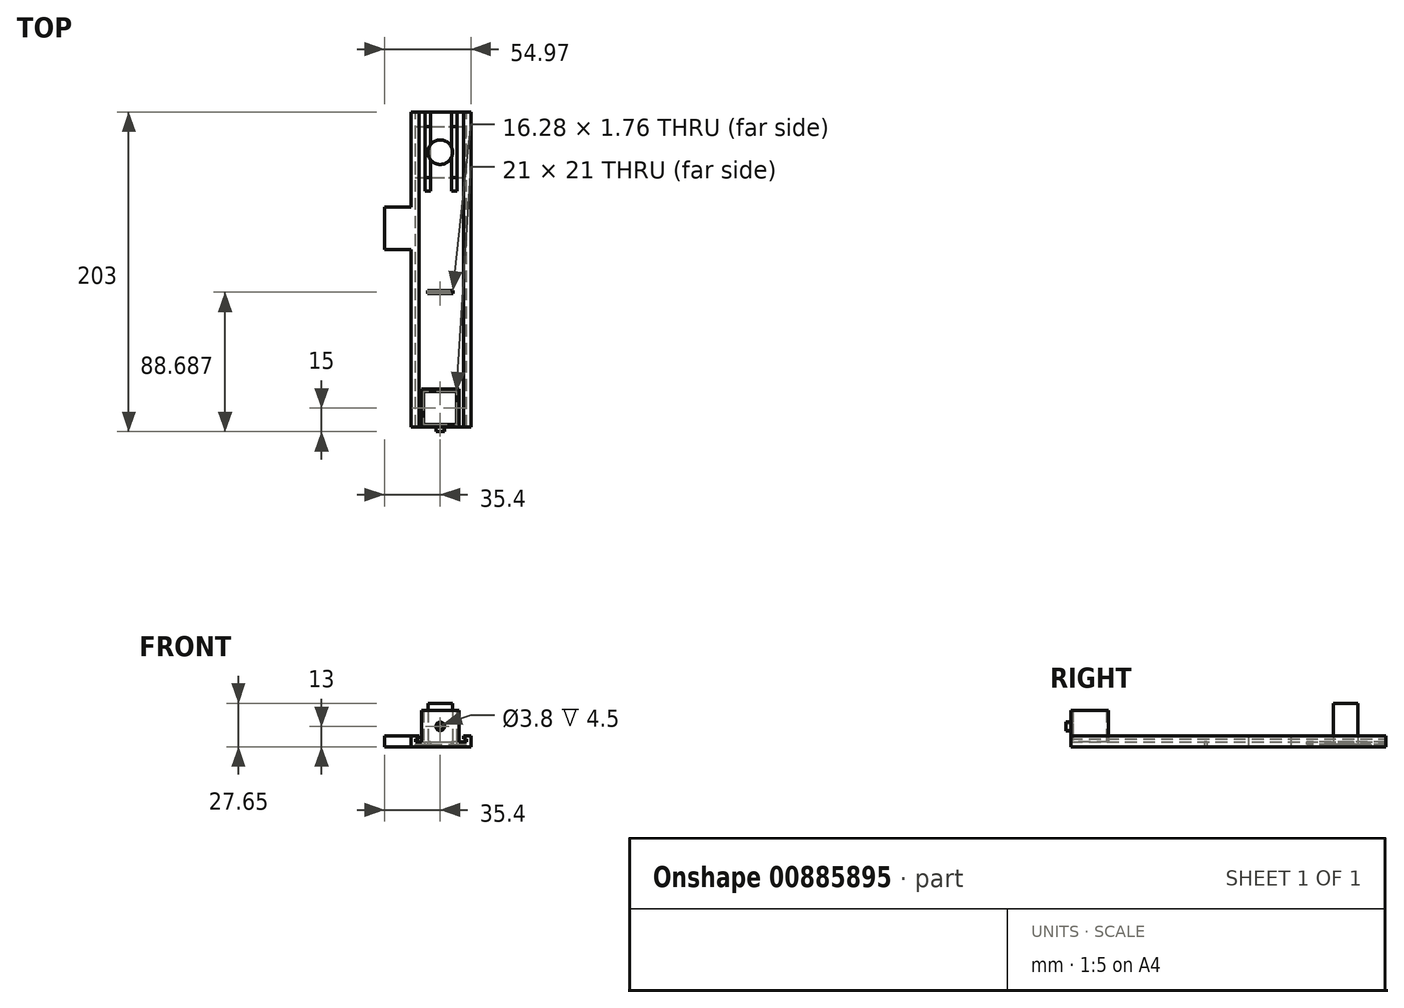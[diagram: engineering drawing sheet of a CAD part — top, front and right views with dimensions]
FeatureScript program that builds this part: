
annotation { "Feature Type Name" : "Feature", "Feature Type Description" : "" }
export const myFeature = defineFeature(function(context is Context, id is Id, definition is map)
    precondition{}
    {
        {
            var Q0;
            Q0=qCreatedBy(makeId("Top.planeOp"),FACE);
            var sketch = newSketch(context, id + "F0", { "sketchPlane" : qUnion([Q0])});
            skLineSegment(sketch, "E0.bottom", {"start": v(-16.12, 16.11) * mm, "end": v(16.13, 16.11) * mm});
            skLineSegment(sketch, "E0.top", {"start": v(-16.13, -16.11) * mm, "end": v(16.12, -16.11) * mm});
            skLineSegment(sketch, "E0.left", {"start": v(-16.12, 16.11) * mm, "end": v(-16.13, -16.11) * mm});
            skLineSegment(sketch, "E0.right", {"start": v(16.13, 16.11) * mm, "end": v(16.12, -16.11) * mm});
            skPoint(sketch, "E0.middle", {"position": v(0, 0) * mm});
            skSolve(sketch);
        }
        {
            var Q0;
            Q0=makeQuery(id+"F0.imprint","IMPRINT",FACE,{"disambiguationData":[TD([[makeQuery(id+"F0.imprint","IMPRINT",EDGE,{"derivedFrom":sQuery(id+"F0.wireOp",EDGE,"E0.bottom")}),-1.0]])]});
            extrude(context, id + "F1", {"entities" : qUnion([Q0]), "depth" : 1.65 * mm, "offsetDistance" : 25 * mm});
        }
        {
            var Q0;
            Q0=makeQuery(id+"F1.opExtrude","CAP_FACE",FACE,{"disambiguationData":[OSD([sQuery(id+"F0.wireOp",EDGE,"E0.bottom"),sQuery(id+"F0.wireOp",EDGE,"E0.top"),sQuery(id+"F0.wireOp",EDGE,"E0.left"),sQuery(id+"F0.wireOp",EDGE,"E0.right")])],"isStart":false});
            var sketch = newSketch(context, id + "F2", { "sketchPlane" : qUnion([Q0])});
            skCircle(sketch, "E1", {"center": v(0, 0) * mm, "radius": 7.8 * mm});
            skSolve(sketch);
        }
        {
            var Q0;
            Q0=makeQuery(id+"F2.imprint","IMPRINT",FACE,{"disambiguationData":[TD([[makeQuery(id+"F2.imprint","IMPRINT",EDGE,{"derivedFrom":sQuery(id+"F2.wireOp",EDGE,"E1")}),1.0]])]});
            extrude(context, id + "F3", {"entities" : qUnion([Q0]), "operationType" : NewBodyOperationType.ADD, "depth" : 26 * mm, "offsetDistance" : 25 * mm});
        }
        {
            var Q0;
            Q0=qCreatedBy(makeId("Top.planeOp"),FACE);
            var sketch = newSketch(context, id + "F4", { "sketchPlane" : qUnion([Q0])});
            skLineSegment(sketch, "E2.bottom", {"start": v(-18.43, 25.4) * mm, "end": v(19.57, 25.4) * mm});
            skLineSegment(sketch, "E2.top", {"start": v(-18.43, -174.6) * mm, "end": v(19.57, -174.6) * mm});
            skLineSegment(sketch, "E2.left", {"start": v(-18.43, 25.4) * mm, "end": v(-18.43, -174.6) * mm});
            skLineSegment(sketch, "E2.right", {"start": v(19.57, 25.4) * mm, "end": v(19.57, -174.6) * mm});
            skSolve(sketch);
        }
        {
            var Q0;
            Q0=makeQuery(id+"F4.imprint","IMPRINT",FACE,{"disambiguationData":[TD([[makeQuery(id+"F4.imprint","IMPRINT",EDGE,{"derivedFrom":sQuery(id+"F4.wireOp",EDGE,"E2.bottom")}),-1.0]])]});
            extrude(context, id + "F5", {"entities" : qUnion([Q0]), "depth" : 3 * mm, "offsetDistance" : 25 * mm});
        }
        {
            var Q0;
            Q0=makeQuery(id+"F5.opExtrude","SWEPT_FACE",FACE,{"disambiguationData":[OSD([sQuery(id+"F4.wireOp",EDGE,"E2.bottom")])]});
            var sketch = newSketch(context, id + "F6", { "sketchPlane" : qUnion([Q0])});
            skLineSegment(sketch, "E3", {"start": v(-0.57, -1.9) * mm, "end": v(-0.57, 4.44) * mm, "construction": true});
            skPoint(sketch, "E3.startSnap0", {"position": v(-0.57, 0) * mm});
            skLineSegment(sketch, "E4", {"start": v(-0.57, 3) * mm, "end": v(-16.72, 3) * mm});
            skLineSegment(sketch, "E5", {"start": v(-16.72, 3) * mm, "end": v(-16.72, 5) * mm});
            skLineSegment(sketch, "E6", {"start": v(-16.72, 5) * mm, "end": v(-14.72, 5) * mm});
            skLineSegment(sketch, "E7", {"start": v(-14.72, 5) * mm, "end": v(-14.72, 7) * mm});
            skLineSegment(sketch, "E8", {"start": v(-14.72, 7) * mm, "end": v(-19.57, 7) * mm});
            skLineSegment(sketch, "E9", {"start": v(-19.57, 7) * mm, "end": v(-19.57, 3) * mm});
            skLineSegment(sketch, "E10", {"start": v(-19.57, 3) * mm, "end": v(-16.72, 3) * mm});
            skLineSegment(sketch, "E11", {"start": v(-0.57, 3) * mm, "end": v(15.58, 3) * mm});
            skLineSegment(sketch, "E12", {"start": v(15.58, 3) * mm, "end": v(15.58, 5) * mm});
            skLineSegment(sketch, "E13", {"start": v(15.58, 5) * mm, "end": v(13.58, 5) * mm});
            skLineSegment(sketch, "E14", {"start": v(13.58, 5) * mm, "end": v(13.58, 7) * mm});
            skLineSegment(sketch, "E15", {"start": v(13.58, 7) * mm, "end": v(18.43, 7) * mm});
            skLineSegment(sketch, "E16", {"start": v(18.43, 7) * mm, "end": v(18.43, 3) * mm});
            skLineSegment(sketch, "E17", {"start": v(18.43, 3) * mm, "end": v(15.58, 3) * mm});
            skSolve(sketch);
        }
        {
            var Q0;
            Q0=makeQuery(id+"F6.imprint","IMPRINT",FACE,{"disambiguationData":[TD([[makeQuery(id+"F6.imprint","IMPRINT",EDGE,{"derivedFrom":sQuery(id+"F6.wireOp",EDGE,"E5")}),1.0]])]});
            var Q1;
            Q1=makeQuery(id+"F6.imprint","IMPRINT",FACE,{"disambiguationData":[TD([[makeQuery(id+"F6.imprint","IMPRINT",EDGE,{"derivedFrom":sQuery(id+"F6.wireOp",EDGE,"E12")}),-1.0]])]});
            var Q2;
            Q2=makeQuery(id+"F5.opExtrude","SWEPT_FACE",FACE,{"disambiguationData":[OSD([sQuery(id+"F4.wireOp",EDGE,"E2.top")])]});
            extrude(context, id + "F7", {"entities" : qUnion([Q0, Q1]), "operationType" : NewBodyOperationType.ADD, "endBound" : BoundingType.UP_TO_SURFACE, "oppositeDirection" : true, "depth" : 25 * mm, "endBoundEntityFace" : qUnion([Q2]), "offsetDistance" : 25 * mm});
        }
        {
            var Q0;
            Q0=makeQuery(id+"F5.opExtrude","CAP_FACE",FACE,{"disambiguationData":[OSD([sQuery(id+"F4.wireOp",EDGE,"E2.bottom"),sQuery(id+"F4.wireOp",EDGE,"E2.top"),sQuery(id+"F4.wireOp",EDGE,"E2.left"),sQuery(id+"F4.wireOp",EDGE,"E2.right")])],"isStart":false});
            var sketch = newSketch(context, id + "F8", { "sketchPlane" : qUnion([Q0])});
            skLineSegment(sketch, "E18", {"start": v(0, -174.6) * mm, "end": v(0, -150.6) * mm, "construction": true});
            skPoint(sketch, "E19.middle", {"position": v(0, -162.6) * mm});
            skLineSegment(sketch, "E20.bottom", {"start": v(-12, -150.6) * mm, "end": v(12, -150.6) * mm});
            skLineSegment(sketch, "E20.top", {"start": v(-12, -174.6) * mm, "end": v(12, -174.6) * mm});
            skLineSegment(sketch, "E20.left", {"start": v(-12, -150.6) * mm, "end": v(-12, -174.6) * mm});
            skLineSegment(sketch, "E20.right", {"start": v(12, -150.6) * mm, "end": v(12, -174.6) * mm});
            skLineSegment(sketch, "E21.bottom", {"start": v(-10.5, -152.1) * mm, "end": v(10.5, -152.1) * mm});
            skLineSegment(sketch, "E21.top", {"start": v(-10.5, -173.1) * mm, "end": v(10.5, -173.1) * mm});
            skLineSegment(sketch, "E21.left", {"start": v(-10.5, -152.1) * mm, "end": v(-10.5, -173.1) * mm});
            skLineSegment(sketch, "E21.right", {"start": v(10.5, -152.1) * mm, "end": v(10.5, -173.1) * mm});
            skSolve(sketch);
        }
        {
            var Q0;
            Q0=makeQuery(id+"F8.imprint","IMPRINT",FACE,{"disambiguationData":[TD([[makeQuery(id+"F8.imprint","IMPRINT",EDGE,{"derivedFrom":sQuery(id+"F8.wireOp",EDGE,"E20.bottom")}),-1.0]])]});
            extrude(context, id + "F9", {"entities" : qUnion([Q0]), "operationType" : NewBodyOperationType.ADD, "depth" : 20 * mm, "offsetDistance" : 25 * mm});
        }
        {
            var Q0;
            {var subQ6=sQuery(id+"F4.wireOp",EDGE,"E2.bottom");var subQ13=sQuery(id+"F4.wireOp",EDGE,"E2.top");Q0=makeQuery(id+"F9.boolean.opBoolean","SPLIT",FACE,{"disambiguationData":[TD([makeQuery(id+"F5.opExtrude","SWEPT_FACE",FACE,{"disambiguationData":[OSD([subQ6])]})])],"derivedFrom":makeQuery(id+"F5.opExtrude","CAP_FACE",FACE,{"disambiguationData":[OSD([subQ6,subQ13,sQuery(id+"F4.wireOp",EDGE,"E2.left"),sQuery(id+"F4.wireOp",EDGE,"E2.right")])],"isStart":false})});}
            var sketch = newSketch(context, id + "F10", { "sketchPlane" : qUnion([Q0])});
            skLineSegment(sketch, "E22.bottom", {"start": v(-18.4, -61.74) * mm, "end": v(-35.4, -61.74) * mm});
            skLineSegment(sketch, "E22.top", {"start": v(-18.4, -34.74) * mm, "end": v(-35.4, -34.74) * mm});
            skLineSegment(sketch, "E22.left", {"start": v(-18.4, -61.74) * mm, "end": v(-18.4, -34.74) * mm});
            skLineSegment(sketch, "E22.right", {"start": v(-35.4, -61.74) * mm, "end": v(-35.4, -34.74) * mm});
            skSolve(sketch);
        }
        {
            var Q0;
            Q0=makeQuery(id+"F10.imprint","IMPRINT",FACE,{"disambiguationData":[TD([[makeQuery(id+"F10.imprint","IMPRINT",EDGE,{"derivedFrom":sQuery(id+"F10.wireOp",EDGE,"E22.bottom")}),-1.0]])]});
            var Q1;
            Q1=makeQuery(id+"F7.opExtrude","SWEPT_FACE",FACE,{"disambiguationData":[OSD([sQuery(id+"F6.wireOp",EDGE,"E15")])]});
            var Q2;
            Q2=makeQuery(id+"F5.opExtrude","CAP_FACE",FACE,{"disambiguationData":[OSD([sQuery(id+"F4.wireOp",EDGE,"E2.bottom"),sQuery(id+"F4.wireOp",EDGE,"E2.top"),sQuery(id+"F4.wireOp",EDGE,"E2.left"),sQuery(id+"F4.wireOp",EDGE,"E2.right")])],"isStart":true});
            extrude(context, id + "F11", {"entities" : qUnion([Q0]), "operationType" : NewBodyOperationType.ADD, "endBound" : BoundingType.UP_TO_SURFACE, "depth" : 4 * mm, "endBoundEntityFace" : qUnion([Q1]), "offsetDistance" : 25 * mm, "hasSecondDirection" : true, "secondDirectionBound" : SecondDirectionBoundingType.UP_TO_SURFACE, "secondDirectionOppositeDirection" : true, "secondDirectionDepth" : 2.7 * mm, "secondDirectionBoundEntityFace" : qUnion([Q2])});
        }
        {
            var Q0;
            Q0=makeQuery(id+"F5.opExtrude","CAP_FACE",FACE,{"disambiguationData":[OSD([sQuery(id+"F4.wireOp",EDGE,"E2.bottom"),sQuery(id+"F4.wireOp",EDGE,"E2.top"),sQuery(id+"F4.wireOp",EDGE,"E2.left"),sQuery(id+"F4.wireOp",EDGE,"E2.right")])],"isStart":true});
            var sketch = newSketch(context, id + "F12", { "sketchPlane" : qUnion([Q0])});
            skLineSegment(sketch, "E23", {"start": v(0.57, 174.6) * mm, "end": v(0, 94.57) * mm, "construction": true});
            skLineSegment(sketch, "E24", {"start": v(0, 94.57) * mm, "end": v(19.57, 94.43) * mm, "construction": true});
            skLineSegment(sketch, "E25.bottom", {"start": v(-8.14, 88.02) * mm, "end": v(8.14, 88.02) * mm});
            skLineSegment(sketch, "E25.top", {"start": v(-8.14, 89.78) * mm, "end": v(8.14, 89.78) * mm});
            skLineSegment(sketch, "E25.left", {"start": v(-8.14, 88.02) * mm, "end": v(-8.14, 89.78) * mm});
            skLineSegment(sketch, "E25.right", {"start": v(8.14, 88.02) * mm, "end": v(8.14, 89.78) * mm});
            skPoint(sketch, "E25.middle", {"position": v(0, 88.9) * mm});
            skSolve(sketch);
        }
        {
            var Q0;
            Q0=makeQuery(id+"F12.imprint","IMPRINT",FACE,{"disambiguationData":[TD([[makeQuery(id+"F12.imprint","IMPRINT",EDGE,{"derivedFrom":sQuery(id+"F12.wireOp",EDGE,"E25.bottom")}),1.0]])]});
            var Q1;
            {var subQ6=sQuery(id+"F4.wireOp",EDGE,"E2.bottom");var subQ13=sQuery(id+"F4.wireOp",EDGE,"E2.top");Q1=makeQuery(id+"F9.boolean.opBoolean","SPLIT",FACE,{"disambiguationData":[TD([makeQuery(id+"F5.opExtrude","SWEPT_FACE",FACE,{"disambiguationData":[OSD([subQ6])]})])],"derivedFrom":makeQuery(id+"F5.opExtrude","CAP_FACE",FACE,{"disambiguationData":[OSD([subQ6,subQ13,sQuery(id+"F4.wireOp",EDGE,"E2.left"),sQuery(id+"F4.wireOp",EDGE,"E2.right")])],"isStart":false})});}
            extrude(context, id + "F13", {"entities" : qUnion([Q0]), "operationType" : NewBodyOperationType.REMOVE, "endBound" : BoundingType.UP_TO_SURFACE, "oppositeDirection" : true, "depth" : 25 * mm, "endBoundEntityFace" : qUnion([Q1]), "offsetDistance" : 25 * mm});
        }
        {
            var Q0;
            {var subQ6=sQuery(id+"F4.wireOp",EDGE,"E2.bottom");var subQ13=sQuery(id+"F4.wireOp",EDGE,"E2.top");Q0=makeQuery(id+"F9.boolean.opBoolean","SPLIT",FACE,{"disambiguationData":[TD([makeQuery(id+"F5.opExtrude","SWEPT_FACE",FACE,{"disambiguationData":[OSD([subQ6])]})])],"derivedFrom":makeQuery(id+"F5.opExtrude","CAP_FACE",FACE,{"disambiguationData":[OSD([subQ6,subQ13,sQuery(id+"F4.wireOp",EDGE,"E2.left"),sQuery(id+"F4.wireOp",EDGE,"E2.right")])],"isStart":false})});}
            var sketch = newSketch(context, id + "F14", { "sketchPlane" : qUnion([Q0])});
            skLineSegment(sketch, "E26", {"start": v(-15.58, 25.4) * mm, "end": v(-9.58, 25.4) * mm, "construction": true});
            skLineSegment(sketch, "E27", {"start": v(-9.58, 25.4) * mm, "end": v(-9.58, -24.6) * mm});
            skLineSegment(sketch, "E28", {"start": v(-9.58, -24.6) * mm, "end": v(-6.18, -24.6) * mm});
            skLineSegment(sketch, "E29", {"start": v(-6.18, -24.6) * mm, "end": v(-6.18, 25.4) * mm});
            skLineSegment(sketch, "E30", {"start": v(-6.18, 25.4) * mm, "end": v(-9.58, 25.4) * mm});
            skLineSegment(sketch, "E31", {"start": v(16.72, 25.4) * mm, "end": v(10.72, 25.4) * mm, "construction": true});
            skLineSegment(sketch, "E32", {"start": v(10.72, 25.4) * mm, "end": v(10.72, -24.6) * mm});
            skLineSegment(sketch, "E33", {"start": v(10.72, -24.6) * mm, "end": v(7.32, -24.6) * mm});
            skLineSegment(sketch, "E34", {"start": v(7.32, -24.6) * mm, "end": v(7.32, 25.4) * mm});
            skLineSegment(sketch, "E35", {"start": v(7.32, 25.4) * mm, "end": v(10.72, 25.4) * mm});
            skSolve(sketch);
        }
        {
            var Q0;
            Q0=makeQuery(id+"F14.imprint","IMPRINT",FACE,{"disambiguationData":[TD([[makeQuery(id+"F14.imprint","IMPRINT",EDGE,{"derivedFrom":sQuery(id+"F14.wireOp",EDGE,"E27")}),1.0]])]});
            var Q1;
            Q1=makeQuery(id+"F14.imprint","IMPRINT",FACE,{"disambiguationData":[TD([[makeQuery(id+"F14.imprint","IMPRINT",EDGE,{"derivedFrom":sQuery(id+"F14.wireOp",EDGE,"E32")}),-1.0]])]});
            extrude(context, id + "F15", {"entities" : qUnion([Q0, Q1]), "operationType" : NewBodyOperationType.REMOVE, "oppositeDirection" : true, "depth" : 1.5 * mm, "offsetDistance" : 25 * mm});
        }
        {
            var Q0;
            Q0=makeQuery(id+"F9.boolean.opBoolean","SPLIT",FACE,{"disambiguationData":[TD([makeQuery(id+"F9.opExtrude","SWEPT_FACE",FACE,{"disambiguationData":[OSD([sQuery(id+"F8.wireOp",EDGE,"E21.bottom")])]})])],"derivedFrom":makeQuery(id+"F5.opExtrude","CAP_FACE",FACE,{"disambiguationData":[OSD([sQuery(id+"F4.wireOp",EDGE,"E2.bottom"),sQuery(id+"F4.wireOp",EDGE,"E2.top"),sQuery(id+"F4.wireOp",EDGE,"E2.left"),sQuery(id+"F4.wireOp",EDGE,"E2.right")])],"isStart":false})});
            extrude(context, id + "F16", {"entities" : qUnion([Q0]), "operationType" : NewBodyOperationType.REMOVE, "endBound" : BoundingType.UP_TO_NEXT, "oppositeDirection" : true, "depth" : 25 * mm, "offsetDistance" : 25 * mm});
        }
        {
            var Q0;
            Q0=makeQuery(id+"F9.boolean.opBoolean","MERGE",FACE,{"derivedFrom":[makeQuery(id+"F7.boolean.opBoolean","MERGE",FACE,{"derivedFrom":[makeQuery(id+"F5.opExtrude","SWEPT_FACE",FACE,{"disambiguationData":[OSD([sQuery(id+"F4.wireOp",EDGE,"E2.top")])]}),makeQuery(id+"F7.opExtrude","CAP_FACE",FACE,{"disambiguationData":[OSD([sQuery(id+"F6.wireOp",EDGE,"E5"),sQuery(id+"F6.wireOp",EDGE,"E6"),sQuery(id+"F6.wireOp",EDGE,"E7"),sQuery(id+"F6.wireOp",EDGE,"E8"),sQuery(id+"F6.wireOp",EDGE,"E9"),sQuery(id+"F6.wireOp",EDGE,"E10")])],"isStart":false}),makeQuery(id+"F7.opExtrude","CAP_FACE",FACE,{"disambiguationData":[OSD([sQuery(id+"F6.wireOp",EDGE,"E12"),sQuery(id+"F6.wireOp",EDGE,"E13"),sQuery(id+"F6.wireOp",EDGE,"E14"),sQuery(id+"F6.wireOp",EDGE,"E15"),sQuery(id+"F6.wireOp",EDGE,"E16"),sQuery(id+"F6.wireOp",EDGE,"E17")])],"isStart":false})]}),makeQuery(id+"F9.opExtrude","SWEPT_FACE",FACE,{"disambiguationData":[OSD([sQuery(id+"F8.wireOp",EDGE,"E20.top")])]})]});
            var sketch = newSketch(context, id + "F17", { "sketchPlane" : qUnion([Q0])});
            skCircle(sketch, "E36", {"center": v(0, 13) * mm, "radius": 2.75 * mm});
            skPoint(sketch, "E36.centerSnap0", {"position": v(-12, 13) * mm});
            skCircle(sketch, "E37", {"center": v(0, 13) * mm, "radius": 1.9 * mm});
            skSolve(sketch);
        }
        {
            var Q0;
            Q0=makeQuery(id+"F17.imprint","IMPRINT",FACE,{"disambiguationData":[TD([[makeQuery(id+"F17.imprint","IMPRINT",EDGE,{"derivedFrom":sQuery(id+"F17.wireOp",EDGE,"E36")}),1.0]])]});
            extrude(context, id + "F18", {"entities" : qUnion([Q0]), "operationType" : NewBodyOperationType.ADD, "depth" : 3 * mm, "offsetDistance" : 25 * mm});
        }
        {
            var Q0;
            Q0=makeQuery(id+"F18.boolean.opBoolean","SPLIT",FACE,{"disambiguationData":[TD([makeQuery(id+"F18.opExtrude","SWEPT_FACE",FACE,{"disambiguationData":[OSD([sQuery(id+"F17.wireOp",EDGE,"E37")])]})])],"derivedFrom":makeQuery(id+"F9.boolean.opBoolean","MERGE",FACE,{"derivedFrom":[makeQuery(id+"F7.boolean.opBoolean","MERGE",FACE,{"derivedFrom":[makeQuery(id+"F5.opExtrude","SWEPT_FACE",FACE,{"disambiguationData":[OSD([sQuery(id+"F4.wireOp",EDGE,"E2.top")])]}),makeQuery(id+"F7.opExtrude","CAP_FACE",FACE,{"disambiguationData":[OSD([sQuery(id+"F6.wireOp",EDGE,"E5"),sQuery(id+"F6.wireOp",EDGE,"E6"),sQuery(id+"F6.wireOp",EDGE,"E7"),sQuery(id+"F6.wireOp",EDGE,"E8"),sQuery(id+"F6.wireOp",EDGE,"E9"),sQuery(id+"F6.wireOp",EDGE,"E10")])],"isStart":false}),makeQuery(id+"F7.opExtrude","CAP_FACE",FACE,{"disambiguationData":[OSD([sQuery(id+"F6.wireOp",EDGE,"E12"),sQuery(id+"F6.wireOp",EDGE,"E13"),sQuery(id+"F6.wireOp",EDGE,"E14"),sQuery(id+"F6.wireOp",EDGE,"E15"),sQuery(id+"F6.wireOp",EDGE,"E16"),sQuery(id+"F6.wireOp",EDGE,"E17")])],"isStart":false})]}),makeQuery(id+"F9.opExtrude","SWEPT_FACE",FACE,{"disambiguationData":[OSD([sQuery(id+"F8.wireOp",EDGE,"E20.top")])]})]})});
            var Q1;
            {var subQ0=sQuery(id+"F8.wireOp",EDGE,"E21.top");Q1=makeQuery(id+"F16.boolean.opBoolean","MERGE",FACE,{"derivedFrom":[makeQuery(id+"F9.opExtrude","SWEPT_FACE",FACE,{"disambiguationData":[OSD([subQ0])]})],"fromTools":[makeQuery(id+"F16.opExtrude","SWEPT_FACE",FACE,{"disambiguationData":[OSD([subQ0])]})]});}
            extrude(context, id + "F19", {"entities" : qUnion([Q0]), "operationType" : NewBodyOperationType.REMOVE, "endBound" : BoundingType.UP_TO_SURFACE, "oppositeDirection" : true, "depth" : 25 * mm, "endBoundEntityFace" : qUnion([Q1]), "offsetDistance" : 25 * mm});
        }
    });
